# Revit family: Bollard-1_800_Bollards-Padlock_Removable-CS3
name_source: partatom
category: Site
revit_build: Autodesk Revit 2017 (Build: 20160225_1515(x64)
units: mm (PartAtom-declared; Revit-internal decimal feet)

## family parameters
Always vertical = Yes
Cut with Voids When Loaded = No
OmniClass Number = 23.15.10.11.21
OmniClass Title = Traffic Safety Barriers and Protections
Part Type = Normal
Round Connector Dimension = Use Diameter
Shared = No
Work Plane-Based = No

## types (7) — shared parameters
Carbon Steel = No
Concrete Finish by others = Concrete, Lightweight
Concrete by others = Yes
Description = Stainless Steel Padlock Removable Bollard
Finish = Metal-1_800_Bollards-Stainless_Steel
Height = 3' - 0"
Manufacturer = 1-800-BOLLARDS
Model = Padlock Removable Bollard
Product Documentation Link = https://microsite.caddetails.com
Product Name = Removable Bollards
Product Page URL = https://1800bollards.com
Rebar by others = Yes
Stainless Steel = Yes
URL = https://1800bollards.com

## per-type parameters (varying)
| type | 10 in Bollard | 12 in Bollard | 3 in Bollard | 4 in Bollard | 5 in Bollard | 6 in Bollard | 8 in Bollard | Assembly Code | Bollard Radius | Dome Height | Foundation Depth | Foundation Width | Height Below Grade | Thickness | Type Comments |
| 3 in | No | No | Yes | No | No | No | No | G2010400 | 0' - 1 3/4" | 0' - 1" | 2' - 0" | 1' - 9" | 1' - 0" | 0' - 3 1/2" | 3 in Nominal Diameter |
| 4 in | No | No | No | Yes | No | No | No | G2010400 | 0' - 2 1/4" | 0' - 1 5/16" | 2' - 0" | 1' - 9" | 1' - 0" | 0' - 4 1/2" | 4 in Nominal Diameter |
| 5 in | No | No | No | No | Yes | No | No | G2010400 | 0' - 2 25/32" | 0' - 1 19/32" | 2' - 0" | 1' - 9" | 1' - 0" | 0' - 5 9/16" | 5 in Nominal Diameter |
| 6 in | No | No | No | No | No | Yes | No | G2020400 | 0' - 3 5/16" | 0' - 1 29/32" | 2' - 0" | 1' - 9" | 1' - 0" | 0' - 6 5/8" | 6 in Nominal Diameter |
| 8 in | No | No | No | No | No | No | Yes | G2040900 | 0' - 4 5/16" | 0' - 2 1/2" | 2' - 0" | 1' - 9" | 1' - 0" | 0' - 8 5/8" | 8 in Nominal Diameter |
| 10 in | Yes | No | No | No | No | No | No | G2010400 | 0' - 5 3/8" | 0' - 3 3/32" | 2' - 0" | 1' - 9" | 1' - 3" | 0' - 10 3/4" | 10 in Nominal Diameter |
| 12 in | No | Yes | No | No | No | No | No | G2010400 | 0' - 6 3/8" | 0' - 3 11/16" | 2' - 6" | 2' - 6" | 1' - 3" | 1' - 0 3/4" | 12 in Nominal Diameter |

## geometry (parser evidence)
native form markers: Sweep x6
no freeform markers — native parametric forms only
